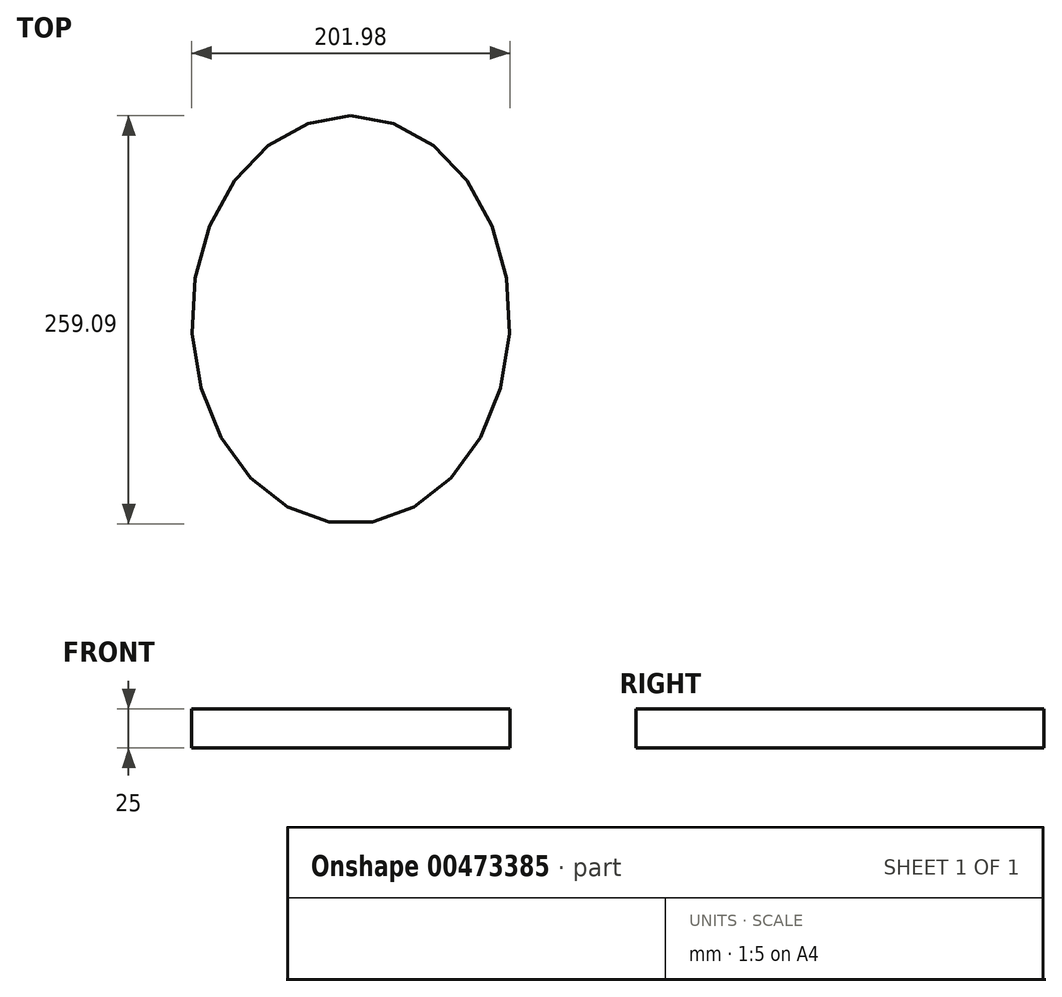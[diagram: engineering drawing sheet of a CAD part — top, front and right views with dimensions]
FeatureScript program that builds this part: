
annotation { "Feature Type Name" : "Feature", "Feature Type Description" : "" }
export const myFeature = defineFeature(function(context is Context, id is Id, definition is map)
    precondition{}
    {
        {
            var Q0;
            Q0=qCreatedBy(makeId("Top.planeOp"),FACE);
            var sketch = newSketch(context, id + "F0", { "sketchPlane" : qUnion([Q0])});
            skEllipse(sketch, "E0", {"center": v(0, 32.96) * mm, "majorRadius": 129.54 * mm, "minorRadius": 101 * mm, "majorAxis": v(0, 1)});
            skSolve(sketch);
        }
        {
            var Q0;
            Q0 = qSketchRegion(id + "F0", true);
            extrude(context, id + "F1", {"entities" : qUnion([Q0]), "depth" : 25 * mm});
        }
    });
